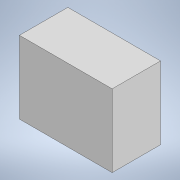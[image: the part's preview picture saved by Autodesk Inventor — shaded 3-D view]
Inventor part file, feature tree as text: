
AUTODESK INVENTOR PART (.ipt)
format: ipt  version: 2020 (Build 240168000, 168)  size: 99,328 bytes
history: native  units: mm
features: extrude x2, imported_body x1, sketch x1
ambient origin geometry x8: Origin, YZ Plane, XZ Plane, XY Plane, X Axis, Y Axis, Z Axis, Center Point
bodies: Solid1 (feature_tree)
feature tree (4):
  extrude  "Extrusion1"  Depth=12.0mm
  extrude  "Extrusion2"  Depth=18.0mm TaperAngle=0.0deg
  imported_body  "base"
  sketch  "Sketch2"  dims[d0=23.0mm d1=12.0mm d2=18.0mm d3=0.0mm d4=3.0mm d5=5.1mm d6=3.0mm d7=9.0mm d8=0.0mm]
